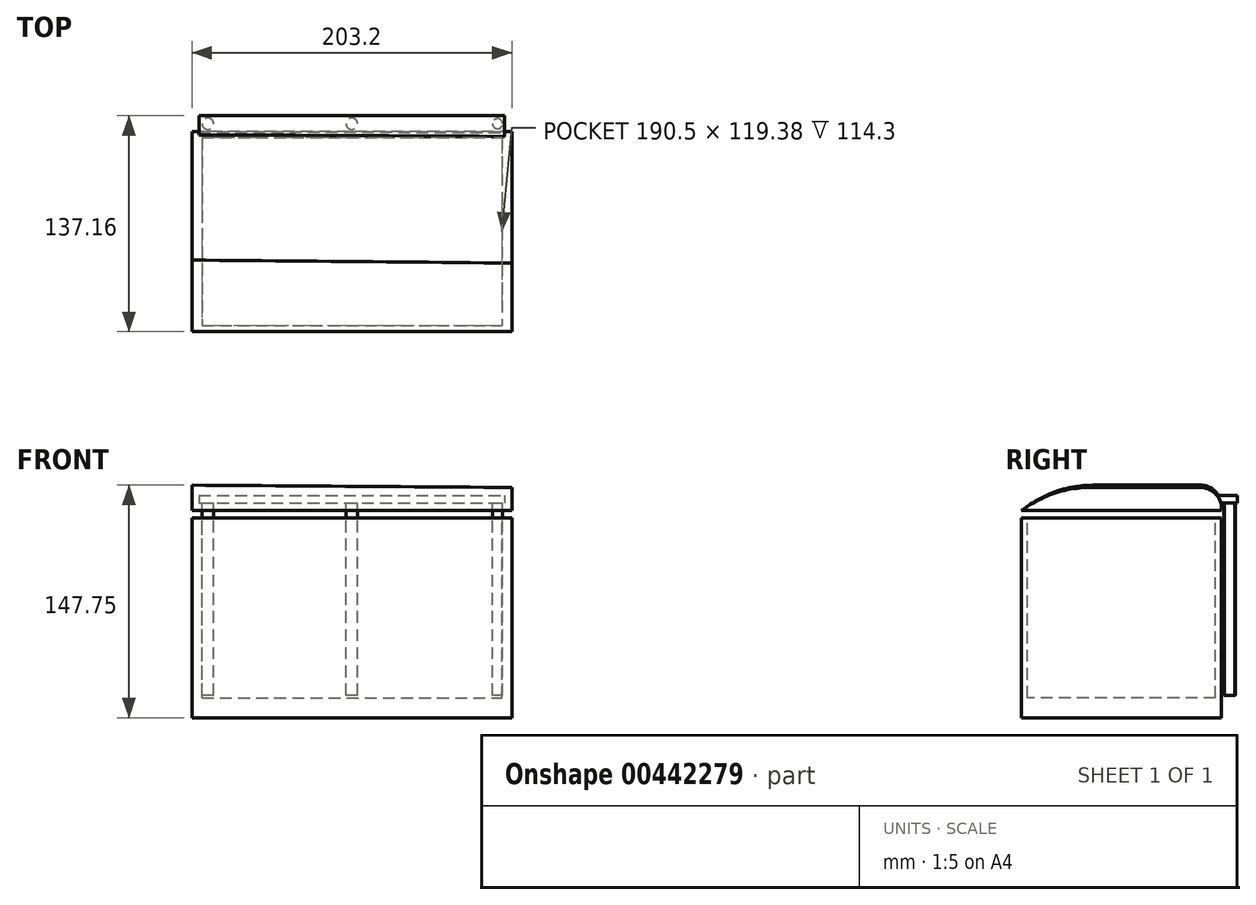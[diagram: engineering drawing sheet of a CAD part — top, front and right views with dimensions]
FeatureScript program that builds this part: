
annotation { "Feature Type Name" : "Feature", "Feature Type Description" : "" }
export const myFeature = defineFeature(function(context is Context, id is Id, definition is map)
    precondition{}
    {
        {
            var Q0;
            Q0=qCreatedBy(makeId("Front.planeOp"),FACE);
            var sketch = newSketch(context, id + "F0", { "sketchPlane" : qUnion([Q0])});
            skLineSegment(sketch, "E0.bottom", {"start": v(-101.6, 63.5) * mm, "end": v(101.6, 63.5) * mm});
            skLineSegment(sketch, "E0.top", {"start": v(-101.6, -63.5) * mm, "end": v(101.6, -63.5) * mm});
            skLineSegment(sketch, "E0.left", {"start": v(-101.6, 63.5) * mm, "end": v(-101.6, -63.5) * mm});
            skLineSegment(sketch, "E0.right", {"start": v(101.6, 63.5) * mm, "end": v(101.6, -63.5) * mm});
            skPoint(sketch, "E0.middle", {"position": v(0, 0) * mm});
            skSolve(sketch);
        }
        {
            var Q0;
            Q0=makeQuery(id+"F0.imprint","IMPRINT",FACE,{"disambiguationData":[TD([[makeQuery(id+"F0.imprint","IMPRINT",EDGE,{"derivedFrom":sQuery(id+"F0.wireOp",EDGE,"E0.bottom")}),-1.0]])]});
            extrude(context, id + "F1", {"entities" : qUnion([Q0]), "endBound" : BoundingType.SYMMETRIC, "depth" : 127 * mm});
        }
        {
            var Q0;
            Q0=makeQuery(id+"F1.opExtrude","SWEPT_FACE",FACE,{"disambiguationData":[OSD([sQuery(id+"F0.wireOp",EDGE,"E0.bottom")])]});
            var sketch = newSketch(context, id + "F2", { "sketchPlane" : qUnion([Q0])});
            skLineSegment(sketch, "E1.bottom", {"start": v(-95.25, 59.7) * mm, "end": v(95.25, 59.7) * mm});
            skLineSegment(sketch, "E1.top", {"start": v(-95.25, -59.7) * mm, "end": v(95.25, -59.7) * mm});
            skLineSegment(sketch, "E1.left", {"start": v(-95.25, 59.7) * mm, "end": v(-95.25, -59.7) * mm});
            skLineSegment(sketch, "E1.right", {"start": v(95.25, 59.7) * mm, "end": v(95.25, -59.7) * mm});
            skPoint(sketch, "E1.middle", {"position": v(0, 0) * mm});
            skSolve(sketch);
        }
        {
            var Q0;
            Q0=makeQuery(id+"F2.imprint","IMPRINT",FACE,{"disambiguationData":[TD([[makeQuery(id+"F2.imprint","IMPRINT",EDGE,{"derivedFrom":sQuery(id+"F2.wireOp",EDGE,"E1.bottom")}),-1.0]])]});
            extrude(context, id + "F3", {"entities" : qUnion([Q0]), "operationType" : NewBodyOperationType.REMOVE, "oppositeDirection" : true, "depth" : 114.3 * mm});
        }
        {
            var Q0;
            Q0=makeQuery(id+"F1.opExtrude","CAP_FACE",FACE,{"disambiguationData":[OSD([sQuery(id+"F0.wireOp",EDGE,"E0.bottom"),sQuery(id+"F0.wireOp",EDGE,"E0.top"),sQuery(id+"F0.wireOp",EDGE,"E0.left"),sQuery(id+"F0.wireOp",EDGE,"E0.right")])],"isStart":false});
            var sketch = newSketch(context, id + "F4", { "sketchPlane" : qUnion([Q0])});
            skLineSegment(sketch, "E2", {"start": v(-101.6, 68.03) * mm, "end": v(-101.6, 84.25) * mm});
            skLineSegment(sketch, "E3", {"start": v(-101.6, 84.25) * mm, "end": v(101.6, 82.78) * mm});
            skLineSegment(sketch, "E4", {"start": v(101.6, 82.78) * mm, "end": v(101.6, 68.03) * mm});
            skLineSegment(sketch, "E5", {"start": v(101.6, 68.03) * mm, "end": v(-101.6, 68.03) * mm});
            skSolve(sketch);
        }
        {
            var Q0;
            Q0=makeQuery(id+"F4.imprint","IMPRINT",FACE,{"disambiguationData":[TD([[makeQuery(id+"F4.imprint","IMPRINT",EDGE,{"derivedFrom":sQuery(id+"F4.wireOp",EDGE,"E2")}),-1.0]])]});
            extrude(context, id + "F5", {"entities" : qUnion([Q0]), "oppositeDirection" : true, "depth" : 127 * mm});
        }
        {
            var Q0;
            Q0=makeQuery(id+"F5.opExtrude","CAP_FACE",FACE,{"disambiguationData":[OSD([sQuery(id+"F4.wireOp",EDGE,"E2"),sQuery(id+"F4.wireOp",EDGE,"E3"),sQuery(id+"F4.wireOp",EDGE,"E4"),sQuery(id+"F4.wireOp",EDGE,"E5")])],"isStart":false});
            var sketch = newSketch(context, id + "F6", { "sketchPlane" : qUnion([Q0])});
            skLineSegment(sketch, "E6.bottom", {"start": v(97.05, 77.78) * mm, "end": v(-97.05, 77.78) * mm});
            skLineSegment(sketch, "E6.top", {"start": v(97.05, 73.02) * mm, "end": v(-97.05, 73.02) * mm});
            skLineSegment(sketch, "E6.left", {"start": v(97.05, 77.78) * mm, "end": v(97.05, 73.02) * mm});
            skLineSegment(sketch, "E6.right", {"start": v(-97.05, 77.78) * mm, "end": v(-97.05, 73.02) * mm});
            skPoint(sketch, "E6.middle", {"position": v(0, 75.4) * mm});
            skPoint(sketch, "E6.middle.positionSnap0", {"position": v(-101.6, 75.4) * mm});
            skPoint(sketch, "E6.centerSnap0", {"position": v(-101.6, 75.4) * mm});
            skSolve(sketch);
        }
        {
            var Q0;
            Q0=makeQuery(id+"F6.imprint","IMPRINT",FACE,{"disambiguationData":[TD([[makeQuery(id+"F6.imprint","IMPRINT",EDGE,{"derivedFrom":sQuery(id+"F6.wireOp",EDGE,"E6.bottom")}),1.0]])]});
            extrude(context, id + "F7", {"entities" : qUnion([Q0]), "operationType" : NewBodyOperationType.ADD, "depth" : 10.16 * mm});
        }
        {
            var Q0;
            Q0=makeQuery(id+"F7.opExtrude","SWEPT_FACE",FACE,{"disambiguationData":[OSD([sQuery(id+"F6.wireOp",EDGE,"E6.bottom")])]});
            var sketch = newSketch(context, id + "F8", { "sketchPlane" : qUnion([Q0])});
            skCircle(sketch, "E7", {"center": v(-91.44, 68.58) * mm, "radius": 3.67 * mm});
            skPoint(sketch, "E7.centerSnap0", {"position": v(-97.05, 68.58) * mm});
            skCircle(sketch, "E8", {"center": v(92.55, 68.58) * mm, "radius": 3.22 * mm});
            skPoint(sketch, "E8.centerSnap0", {"position": v(97.05, 68.58) * mm});
            skSolve(sketch);
        }
        {
            var Q0;
            Q0=makeQuery(id+"F8.imprint","IMPRINT",FACE,{"disambiguationData":[TD([[makeQuery(id+"F8.imprint","IMPRINT",EDGE,{"derivedFrom":sQuery(id+"F8.wireOp",EDGE,"E7")}),1.0]])]});
            var Q1;
            Q1=makeQuery(id+"F8.imprint","IMPRINT",FACE,{"disambiguationData":[TD([[makeQuery(id+"F8.imprint","IMPRINT",EDGE,{"derivedFrom":sQuery(id+"F8.wireOp",EDGE,"E8")}),1.0]])]});
            extrude(context, id + "F9", {"entities" : qUnion([Q0, Q1]), "operationType" : NewBodyOperationType.ADD, "oppositeDirection" : true, "depth" : 127 * mm});
        }
        {
            var Q0;
            Q0=makeQuery(id+"F7.opExtrude","SWEPT_FACE",FACE,{"disambiguationData":[OSD([sQuery(id+"F6.wireOp",EDGE,"E6.bottom")])]});
            var sketch = newSketch(context, id + "F10", { "sketchPlane" : qUnion([Q0])});
            skCircle(sketch, "E9", {"center": v(0, 68.58) * mm, "radius": 3.65 * mm});
            skPoint(sketch, "E9.centerSnap0", {"position": v(-97.05, 68.58) * mm});
            skPoint(sketch, "E9.centerSnap1", {"position": v(0, 63.5) * mm});
            skSolve(sketch);
        }
        {
            var Q0;
            Q0=makeQuery(id+"F10.imprint","IMPRINT",FACE,{"disambiguationData":[TD([[makeQuery(id+"F10.imprint","IMPRINT",EDGE,{"derivedFrom":sQuery(id+"F10.wireOp",EDGE,"E9")}),1.0]])]});
            extrude(context, id + "F11", {"entities" : qUnion([Q0]), "operationType" : NewBodyOperationType.ADD, "oppositeDirection" : true, "depth" : 127 * mm});
        }
        {
            var Q0;
            Q0=makeQuery(id+"F5.opExtrude","CAP_EDGE",EDGE,{"disambiguationData":[OSD([sQuery(id+"F4.wireOp",EDGE,"E3")])],"isStart":true});
            fillet(context, id + "F12", {"entities" : qUnion([Q0]), "radius" : 71.75 * mm, "tangentPropagation" : true, "allowEdgeOverflow" : false});
        }
        {
            var Q0;
            Q0=makeQuery(id+"F5.opExtrude","CAP_EDGE",EDGE,{"disambiguationData":[OSD([sQuery(id+"F4.wireOp",EDGE,"E3")])],"isStart":false});
            fillet(context, id + "F13", {"entities" : qUnion([Q0]), "radius" : 13.5 * mm, "tangentPropagation" : true, "allowEdgeOverflow" : false});
        }
    });
